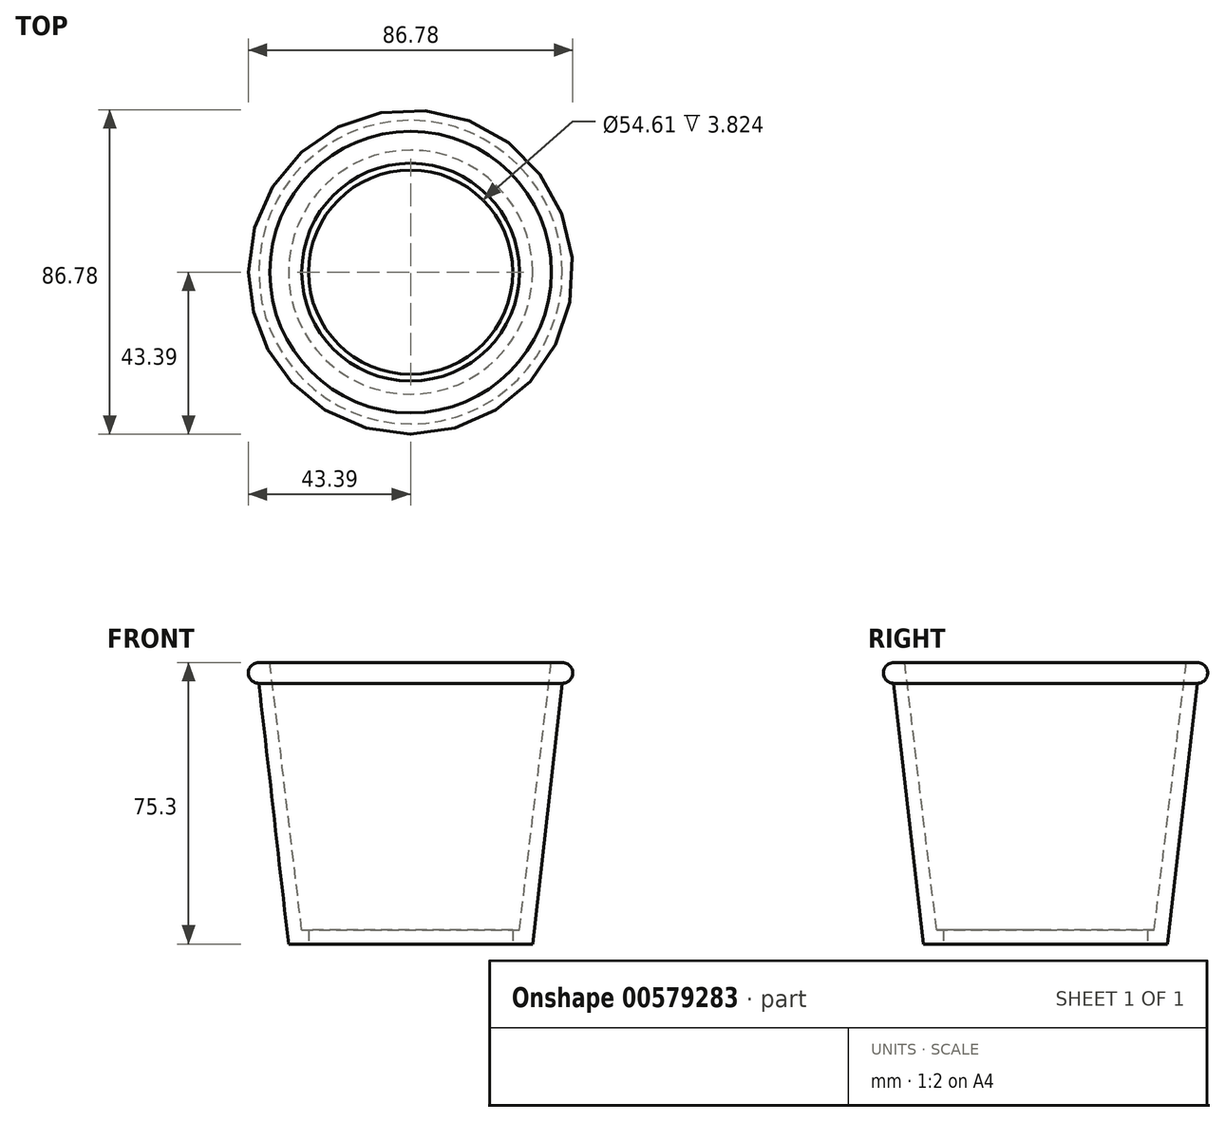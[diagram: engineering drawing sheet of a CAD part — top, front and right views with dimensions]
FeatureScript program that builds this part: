
annotation { "Feature Type Name" : "Feature", "Feature Type Description" : "" }
export const myFeature = defineFeature(function(context is Context, id is Id, definition is map)
    precondition{}
    {
        {
            var Q0;
            Q0=qCreatedBy(makeId("Front.planeOp"),FACE);
            var sketch = newSketch(context, id + "F0", { "sketchPlane" : qUnion([Q0])});
            skLineSegment(sketch, "E0", {"start": v(-40.6, 39.12) * mm, "end": v(-32.65, -30.6) * mm});
            skLineSegment(sketch, "E1", {"start": v(-32.65, -30.6) * mm, "end": v(0, -30.6) * mm});
            skLineSegment(sketch, "E2", {"start": v(0, -30.6) * mm, "end": v(0, -26.77) * mm});
            skArc(sketch, "E3", {"start": v(-40.6, 44.71) * mm, "mid": v(-43.39, 41.92) * mm, "end": v(-40.6, 39.12) * mm});
            skLineSegment(sketch, "E4", {"start": v(-40.6, 44.71) * mm, "end": v(-37.65, 44.71) * mm});
            skLineSegment(sketch, "E5", {"start": v(-37.65, 44.71) * mm, "end": v(-29.12, -26.77) * mm});
            skLineSegment(sketch, "E6", {"start": v(-29.12, -26.77) * mm, "end": v(0, -26.77) * mm});
            skPoint(sketch, "E7.orphan", {"position": v(0, 44.71) * mm});
            skSolve(sketch);
        }
        {
            var Q0;
            Q0=makeQuery(id+"F0.imprint","IMPRINT",FACE,{"disambiguationData":[TD([[makeQuery(id+"F0.imprint","IMPRINT",EDGE,{"derivedFrom":sQuery(id+"F0.wireOp",EDGE,"E0")}),1.0]])]});
            var Q1;
            Q1=sQuery(id+"F0.wireOp",EDGE,"E2");
            revolve(context, id + "F1", {"entities" : qUnion([Q0]), "axis" : qUnion([Q1]), "revolveType" : RevolveType.FULL});
        }
        {
            var Q0;
            Q0=makeQuery(id+"F1.opRevolve","SWEPT_FACE",FACE,{"disambiguationData":[OSD([sQuery(id+"F0.wireOp",EDGE,"E1")])]});
            var sketch = newSketch(context, id + "F2", { "sketchPlane" : qUnion([Q0])});
            skCircle(sketch, "E8", {"center": v(0, 0) * mm, "radius": 27.3 * mm});
            skSolve(sketch);
        }
        {
            var Q0;
            Q0=makeQuery(id+"F2.imprint","IMPRINT",FACE,{"disambiguationData":[TD([[makeQuery(id+"F2.imprint","IMPRINT",EDGE,{"derivedFrom":sQuery(id+"F2.wireOp",EDGE,"E8")}),1.0]])]});
            extrude(context, id + "F3", {"entities" : qUnion([Q0]), "operationType" : NewBodyOperationType.REMOVE, "oppositeDirection" : true, "depth" : 5.84 * mm, "offsetDistance" : 25.4 * mm});
        }
    });
